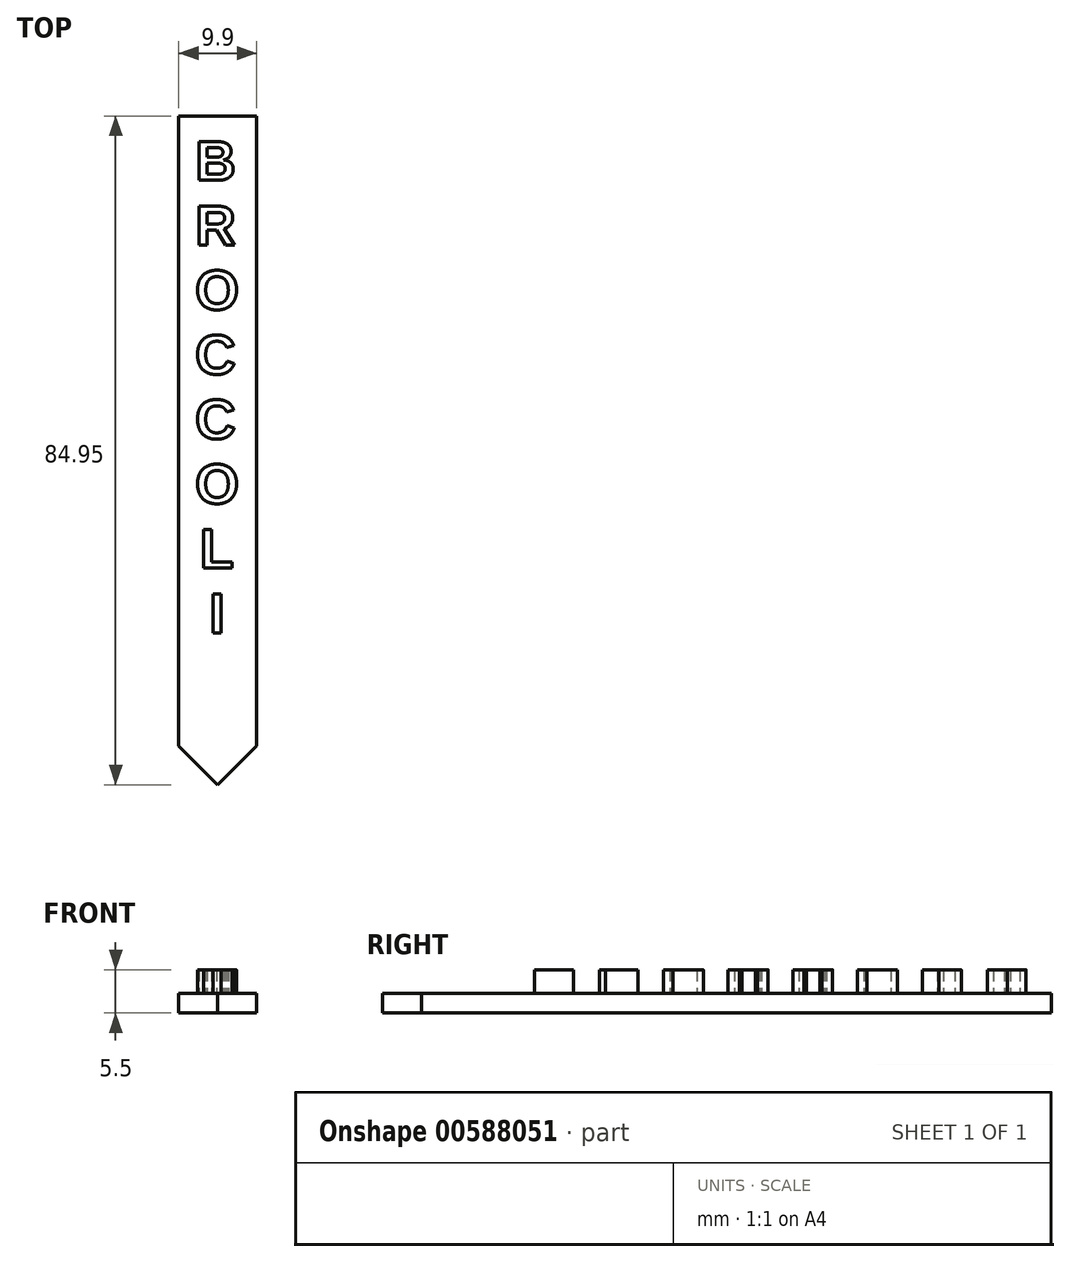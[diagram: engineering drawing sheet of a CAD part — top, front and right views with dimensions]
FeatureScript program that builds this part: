
annotation { "Feature Type Name" : "Feature", "Feature Type Description" : "" }
export const myFeature = defineFeature(function(context is Context, id is Id, definition is map)
    precondition{}
    {
        {
            var Q0;
            Q0=qCreatedBy(makeId("Top.planeOp"),FACE);
            var sketch = newSketch(context, id + "F0", { "sketchPlane" : qUnion([Q0])});
            skLineSegment(sketch, "E0", {"start": v(0, 0) * mm, "end": v(4.95, 4.95) * mm});
            skLineSegment(sketch, "E1", {"start": v(0, 0) * mm, "end": v(-4.95, 4.95) * mm});
            skPoint(sketch, "E2.end.orphan", {"position": v(-3.53, 0) * mm});
            skPoint(sketch, "E3.end.orphan", {"position": v(4.95, 0) * mm});
            skLineSegment(sketch, "E4", {"start": v(4.95, 4.95) * mm, "end": v(4.95, 84.95) * mm});
            skLineSegment(sketch, "E5", {"start": v(-4.95, 4.95) * mm, "end": v(-4.95, 84.95) * mm});
            skLineSegment(sketch, "E6", {"start": v(-4.95, 84.95) * mm, "end": v(4.95, 84.95) * mm});
            skSolve(sketch);
        }
        {
            var Q0;
            Q0=qSketchRegion(id+"F0",true);
            extrude(context, id + "F1", {"entities" : qUnion([Q0]), "depth" : 2.5 * mm, "offsetDistance" : 25 * mm});
        }
        {
            var Q0;
            Q0=makeQuery(id+"F1.opExtrude","CAP_FACE",FACE,{"disambiguationData":[OSD([sQuery(id+"F0.wireOp",EDGE,"E0"),sQuery(id+"F0.wireOp",EDGE,"E1"),sQuery(id+"F0.wireOp",EDGE,"E4"),sQuery(id+"F0.wireOp",EDGE,"E5"),sQuery(id+"F0.wireOp",EDGE,"E6")])],"isStart":false});
            var sketch = newSketch(context, id + "F2", { "sketchPlane" : qUnion([Q0])});
            skText(sketch, "E7", { "text": "B\nR\nO\nC\nC\nO\n\n", "fontName": "Arimo-Bold.ttf"});
            skText(sketch, "E8", { "text": "I", "fontName": "Arimo-Bold.ttf"});
            skText(sketch, "E9", { "text": "L", "fontName": "Arimo-Bold.ttf"});
            const initialGuessF2  = {"E7": [-0.00286, 0.0768, 1, 0, 0.00514], "E8": [-0.00108, 0.01926, 1, 0, 0.0052], "E9": [-0.0023, 0.02753, 1, 0, 0.00511]};
            skSetInitialGuess(sketch, initialGuessF2);
            skSolve(sketch);
        }
        {
            var Q0;
            Q0=qSketchRegion(id+"F2",true);
            extrude(context, id + "F3", {"entities" : qUnion([Q0]), "operationType" : NewBodyOperationType.ADD, "depth" : 3 * mm, "offsetDistance" : 25 * mm});
        }
    });
